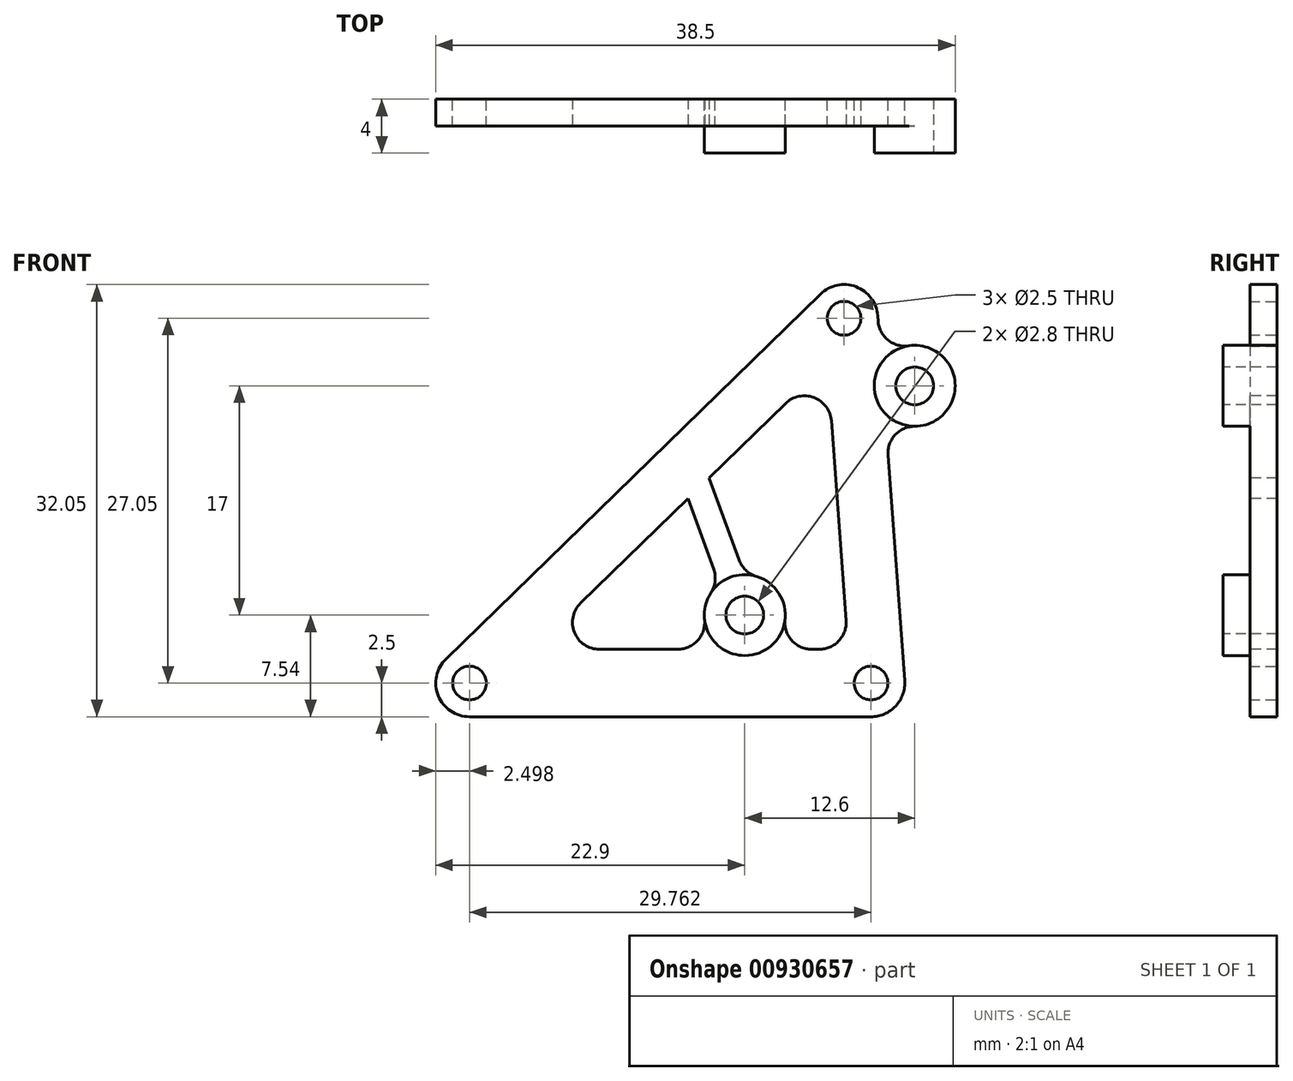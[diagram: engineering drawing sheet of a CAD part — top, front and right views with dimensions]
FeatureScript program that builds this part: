
annotation { "Feature Type Name" : "Feature", "Feature Type Description" : "" }
export const myFeature = defineFeature(function(context is Context, id is Id, definition is map)
    precondition{}
    {
        {
            var Q0;
            Q0=qCreatedBy(makeId("Front.planeOp"),FACE);
            var sketch = newSketch(context, id + "F0", { "sketchPlane" : qUnion([Q0])});
            skLineSegment(sketch, "E0.bottom", {"start": v(0, 0) * mm, "end": v(19.9, 0) * mm, "construction": true});
            skLineSegment(sketch, "E0.top", {"start": v(0, 22.1) * mm, "end": v(19.9, 22.1) * mm, "construction": true});
            skLineSegment(sketch, "E0.left", {"start": v(0, 0) * mm, "end": v(0, 22.1) * mm, "construction": true});
            skLineSegment(sketch, "E0.right", {"start": v(19.9, 0) * mm, "end": v(19.9, 22.1) * mm, "construction": true});
            skCircle(sketch, "E1", {"center": v(8.84, 11.04) * mm, "radius": 8.2 * mm, "construction": true});
            skCircle(sketch, "E2", {"center": v(15.14, 19.54) * mm, "radius": 1.55 * mm, "construction": true});
            skCircle(sketch, "E3", {"center": v(2.54, 2.54) * mm, "radius": 1.55 * mm, "construction": true});
            skLineSegment(sketch, "E4.bottom", {"start": v(-21.86, 25) * mm, "end": v(-2, 25) * mm, "construction": true});
            skLineSegment(sketch, "E4.top", {"start": v(-21.86, 0) * mm, "end": v(-2, 0) * mm, "construction": true});
            skLineSegment(sketch, "E4.left", {"start": v(-23.86, 23) * mm, "end": v(-23.86, 2) * mm, "construction": true});
            skLineSegment(sketch, "E4.right", {"start": v(0, 23) * mm, "end": v(0, 2) * mm, "construction": true});
            skArc(sketch, "E5", {"start": v(-21.86, 25) * mm, "mid": v(-23.28, 24.41) * mm, "end": v(-23.86, 23) * mm, "construction": true});
            skArc(sketch, "E6", {"start": v(0, 23) * mm, "mid": v(-0.59, 24.41) * mm, "end": v(-2, 25) * mm, "construction": true});
            skArc(sketch, "E7", {"start": v(-23.86, 2) * mm, "mid": v(-23.28, 0.59) * mm, "end": v(-21.86, 0) * mm, "construction": true});
            skArc(sketch, "E8", {"start": v(-2, 0) * mm, "mid": v(-0.59, 0.59) * mm, "end": v(0, 2) * mm, "construction": true});
            skCircle(sketch, "E9", {"center": v(-14.5, 23) * mm, "radius": 1.1 * mm, "construction": true});
            skCircle(sketch, "E10", {"center": v(-2, 23) * mm, "radius": 1.1 * mm, "construction": true});
            skCircle(sketch, "E11", {"center": v(-2, 2) * mm, "radius": 1.1 * mm, "construction": true});
            skCircle(sketch, "E12", {"center": v(-14.5, 2) * mm, "radius": 1.1 * mm, "construction": true});
            skCircle(sketch, "E13", {"center": v(-14.4, 12.5) * mm, "radius": 3.7 * mm, "construction": true});
            skLineSegment(sketch, "E14.bottom", {"start": v(-18.65, 16.75) * mm, "end": v(-10.15, 16.75) * mm, "construction": true});
            skLineSegment(sketch, "E14.top", {"start": v(-18.65, 8.25) * mm, "end": v(-10.15, 8.25) * mm, "construction": true});
            skLineSegment(sketch, "E14.left", {"start": v(-18.65, 16.75) * mm, "end": v(-18.65, 8.25) * mm, "construction": true});
            skLineSegment(sketch, "E14.right", {"start": v(-10.15, 16.75) * mm, "end": v(-10.15, 8.25) * mm, "construction": true});
            skLineSegment(sketch, "E15", {"start": v(-23.86, 20.5) * mm, "end": v(-31.86, 20.5) * mm, "construction": true});
            skLineSegment(sketch, "E16", {"start": v(-31.86, 20.5) * mm, "end": v(-31.86, 4.5) * mm, "construction": true});
            skLineSegment(sketch, "E17", {"start": v(-31.86, 4.5) * mm, "end": v(-23.86, 4.5) * mm, "construction": true});
            skSolve(sketch);
        }
        {
            var Q0;
            Q0=qCreatedBy(makeId("Front.planeOp"),FACE);
            var sketch = newSketch(context, id + "F1", { "sketchPlane" : qUnion([Q0])});
            skCircle(sketch, "E18", {"center": v(-17.86, -2.5) * mm, "radius": 2 * mm, "construction": true});
            skCircle(sketch, "E19", {"center": v(11.9, -2.5) * mm, "radius": 2 * mm, "construction": true});
            skCircle(sketch, "E20", {"center": v(9.9, 24.55) * mm, "radius": 2 * mm, "construction": true});
            skLineSegment(sketch, "E21.top", {"start": v(-17.86, -5) * mm, "end": v(11.9, -5) * mm});
            skCircle(sketch, "E22", {"center": v(-17.86, -2.5) * mm, "radius": 1.25 * mm});
            skCircle(sketch, "E23", {"center": v(11.9, -2.5) * mm, "radius": 1.25 * mm});
            skCircle(sketch, "E24", {"center": v(9.9, 24.55) * mm, "radius": 1.25 * mm});
            skLineSegment(sketch, "E25", {"start": v(-19.6, -0.7) * mm, "end": v(8.16, 26.34) * mm});
            skArc(sketch, "E26", {"start": v(-19.6, -0.7) * mm, "mid": v(-20.18, -3.44) * mm, "end": v(-17.86, -5) * mm});
            skArc(sketch, "E27", {"start": v(11.9, -5) * mm, "mid": v(13.73, -4.2) * mm, "end": v(14.4, -2.32) * mm});
            skArc(sketch, "E28", {"start": v(15.15, 16.54) * mm, "mid": v(18.13, 19.76) * mm, "end": v(14.7, 22.5) * mm});
            skArc(sketch, "E29", {"start": v(12.4, 24.73) * mm, "mid": v(10.79, 26.89) * mm, "end": v(8.16, 26.34) * mm});
            skLineSegment(sketch, "E30", {"start": v(12.4, 24.73) * mm, "end": v(12.42, 24.34) * mm});
            skLineSegment(sketch, "E31.trimOffspring", {"start": v(13.16, 14.4) * mm, "end": v(14.4, -2.32) * mm});
            skArc(sketch, "E32", {"start": v(12.42, 24.34) * mm, "mid": v(13.17, 22.93) * mm, "end": v(14.7, 22.5) * mm});
            skArc(sketch, "E33", {"start": v(15.15, 16.54) * mm, "mid": v(13.69, 15.9) * mm, "end": v(13.16, 14.4) * mm});
            skSolve(sketch);
        }
        {
            var Q0;
            Q0=qSketchRegion(id+"F1",true);
            extrude(context, id + "F2", {"entities" : qUnion([Q0]), "depth" : 2 * mm, "offsetDistance" : 25 * mm});
        }
        {
            var Q0;
            Q0=makeQuery(id+"F2.opExtrude","CAP_FACE",FACE,{"disambiguationData":[OSD([sQuery(id+"F1.wireOp",EDGE,"E21.top"),sQuery(id+"F1.wireOp",EDGE,"E22"),sQuery(id+"F1.wireOp",EDGE,"E23"),sQuery(id+"F1.wireOp",EDGE,"E24"),sQuery(id+"F1.wireOp",EDGE,"E25"),sQuery(id+"F1.wireOp",EDGE,"E26"),sQuery(id+"F1.wireOp",EDGE,"E27"),sQuery(id+"F1.wireOp",EDGE,"E28"),sQuery(id+"F1.wireOp",EDGE,"E29"),sQuery(id+"F1.wireOp",EDGE,"E30"),sQuery(id+"F1.wireOp",EDGE,"E31.trimOffspring"),sQuery(id+"F1.wireOp",EDGE,"E32"),sQuery(id+"F1.wireOp",EDGE,"E33")])],"isStart":false});
            var sketch = newSketch(context, id + "F3", { "sketchPlane" : qUnion([Q0])});
            skCircle(sketch, "E34", {"center": v(15.14, 19.54) * mm, "radius": 3 * mm});
            skCircle(sketch, "E35", {"center": v(2.54, 2.54) * mm, "radius": 3 * mm});
            skSolve(sketch);
        }
        {
            var Q0;
            Q0=qSketchRegion(id+"F3",true);
            extrude(context, id + "F4", {"entities" : qUnion([Q0]), "operationType" : NewBodyOperationType.ADD, "depth" : 2 * mm, "offsetDistance" : 25 * mm});
        }
        {
            var Q0;
            Q0=makeQuery(id+"F4.opExtrude","CAP_FACE",FACE,{"disambiguationData":[OSD([sQuery(id+"F3.wireOp",EDGE,"E34")])],"isStart":false});
            var sketch = newSketch(context, id + "F5", { "sketchPlane" : qUnion([Q0])});
            skCircle(sketch, "E36", {"center": v(15.14, 19.54) * mm, "radius": 1.4 * mm});
            skCircle(sketch, "E37", {"center": v(2.54, 2.54) * mm, "radius": 1.4 * mm});
            skSolve(sketch);
        }
        {
            var Q0;
            Q0=qSketchRegion(id+"F5",true);
            extrude(context, id + "F6", {"entities" : qUnion([Q0]), "operationType" : NewBodyOperationType.REMOVE, "endBound" : BoundingType.UP_TO_NEXT, "oppositeDirection" : true, "depth" : 25 * mm, "offsetDistance" : 25 * mm});
        }
        {
            var Q0;
            Q0=makeQuery(id+"F2.opExtrude","CAP_FACE",FACE,{"disambiguationData":[OSD([sQuery(id+"F1.wireOp",EDGE,"E21.top"),sQuery(id+"F1.wireOp",EDGE,"E22"),sQuery(id+"F1.wireOp",EDGE,"E23"),sQuery(id+"F1.wireOp",EDGE,"E24"),sQuery(id+"F1.wireOp",EDGE,"E25"),sQuery(id+"F1.wireOp",EDGE,"E26"),sQuery(id+"F1.wireOp",EDGE,"E27"),sQuery(id+"F1.wireOp",EDGE,"E28"),sQuery(id+"F1.wireOp",EDGE,"E29"),sQuery(id+"F1.wireOp",EDGE,"E30"),sQuery(id+"F1.wireOp",EDGE,"E31.trimOffspring"),sQuery(id+"F1.wireOp",EDGE,"E32"),sQuery(id+"F1.wireOp",EDGE,"E33")])],"isStart":false});
            var sketch = newSketch(context, id + "F7", { "sketchPlane" : qUnion([Q0])});
            skLineSegment(sketch, "E38", {"start": v(-9.62, 3.43) * mm, "end": v(-1.67, 11.18) * mm});
            skLineSegment(sketch, "E39", {"start": v(8.96, 16.95) * mm, "end": v(10.05, 2.15) * mm});
            skLineSegment(sketch, "E40", {"start": v(2.54, 2.54) * mm, "end": v(-0.88, 11.95) * mm, "construction": true});
            skLineSegment(sketch, "E41", {"start": v(-8.23, 0) * mm, "end": v(-2.43, 0) * mm});
            skLineSegment(sketch, "E42", {"start": v(7.51, 0) * mm, "end": v(8.06, 0) * mm});
            skLineSegment(sketch, "E43", {"start": v(-0.1, 12.71) * mm, "end": v(2.51, 5.54) * mm});
            skLineSegment(sketch, "E44", {"start": v(-1.67, 11.18) * mm, "end": v(0.63, 4.86) * mm});
            skArc(sketch, "E45", {"start": v(-9.62, 3.43) * mm, "mid": v(-10.08, 1.25) * mm, "end": v(-8.23, 0) * mm});
            skArc(sketch, "E46", {"start": v(8.96, 16.95) * mm, "mid": v(7.67, 18.67) * mm, "end": v(5.57, 18.23) * mm});
            skArc(sketch, "E47", {"start": v(8.06, 0) * mm, "mid": v(9.52, 0.64) * mm, "end": v(10.05, 2.15) * mm});
            skArc(sketch, "E48", {"start": v(-2.43, 0) * mm, "mid": v(-0.94, 0.66) * mm, "end": v(-0.44, 2.22) * mm});
            skArc(sketch, "E49", {"start": v(0.63, 4.86) * mm, "mid": v(-0.24, 3.67) * mm, "end": v(-0.44, 2.22) * mm});
            skArc(sketch, "E50", {"start": v(5.52, 2.22) * mm, "mid": v(6.02, 0.66) * mm, "end": v(7.51, 0) * mm});
            skArc(sketch, "E51", {"start": v(5.52, 2.22) * mm, "mid": v(4.76, 4.55) * mm, "end": v(2.51, 5.54) * mm});
            skLineSegment(sketch, "E52.trimOffspring", {"start": v(-0.1, 12.71) * mm, "end": v(5.57, 18.23) * mm});
            skSolve(sketch);
        }
        {
            var Q0;
            Q0=qSketchRegion(id+"F7",true);
            extrude(context, id + "F8", {"entities" : qUnion([Q0]), "operationType" : NewBodyOperationType.REMOVE, "endBound" : BoundingType.UP_TO_NEXT, "oppositeDirection" : true, "depth" : 25 * mm, "offsetDistance" : 25 * mm});
        }
        {
            var Q0;
            Q0=makeQuery(id+"F8.boolean.opBoolean","COPY",EDGE,{"derivedFrom":makeQuery(id+"F8.opExtrude","SWEPT_EDGE",EDGE,{"disambiguationData":[OSD([sQuery(id+"F3.wireOp",EDGE,"hXc8IJ8Q-pLij-LfgQ-s92c-YovqnbquMZ1k"),sQuery(id+"F7.wireOp",EDGE,"E44"),sQuery(id+"F7.wireOp",EDGE,"E49")])]})});
            var Q1;
            Q1=makeQuery(id+"F8.boolean.opBoolean","COPY",EDGE,{"derivedFrom":makeQuery(id+"F8.opExtrude","SWEPT_EDGE",EDGE,{"disambiguationData":[OSD([sQuery(id+"F3.wireOp",EDGE,"hXc8IJ8Q-pLij-LfgQ-s92c-YovqnbquMZ1k"),sQuery(id+"F7.wireOp",EDGE,"E43"),sQuery(id+"F7.wireOp",EDGE,"E51")])]})});
            fillet(context, id + "F9", {"entities" : qUnion([Q0, Q1]), "radius" : 2 * mm, "tangentPropagation" : true, "allowEdgeOverflow" : false});
        }
    });
